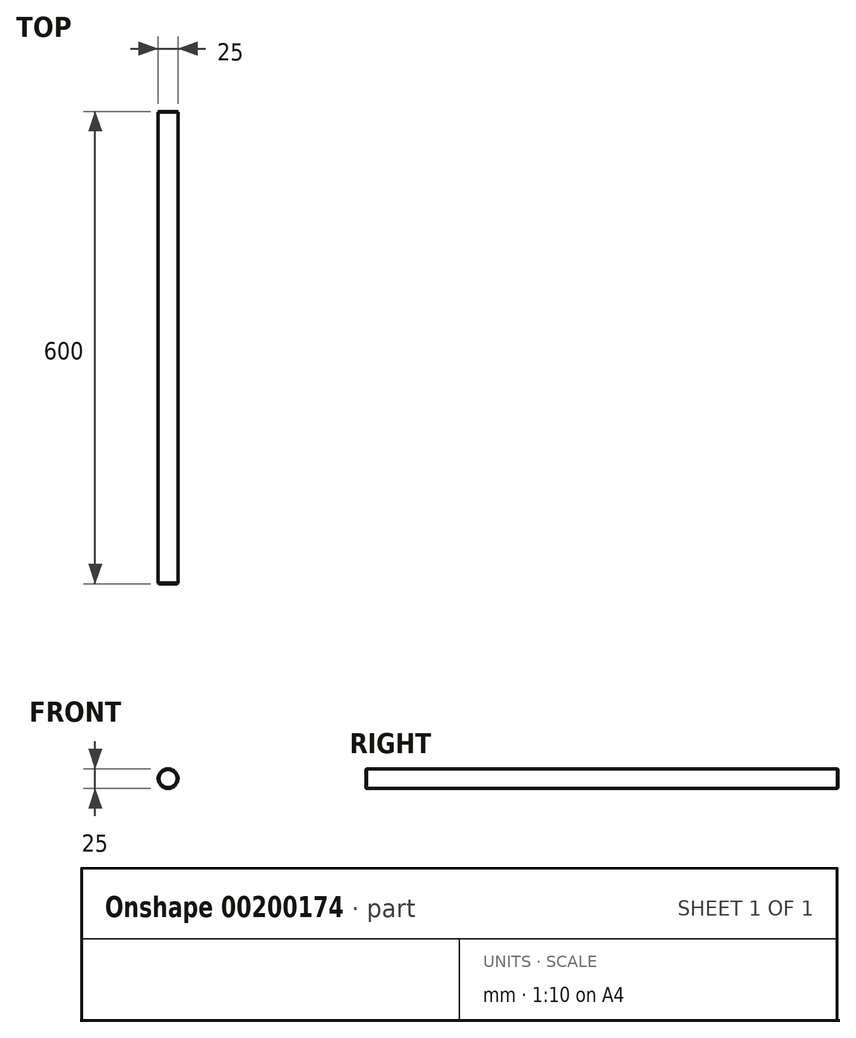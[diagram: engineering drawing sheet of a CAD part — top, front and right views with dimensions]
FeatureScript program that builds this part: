
annotation { "Feature Type Name" : "Feature", "Feature Type Description" : "" }
export const myFeature = defineFeature(function(context is Context, id is Id, definition is map)
    precondition{}
    {
        {
            var Q0;
            Q0=qCreatedBy(makeId("Front.planeOp"),FACE);
            var sketch = newSketch(context, id + "F0", { "sketchPlane" : qUnion([Q0])});
            skCircle(sketch, "E0", {"center": v(0, 0) * mm, "radius": 12.5 * mm});
            skSolve(sketch);
        }
        {
            var Q0;
            Q0 = qSketchRegion(id + "F0", true);
            extrude(context, id + "F1", {"entities" : qUnion([Q0]), "depth" : 600 * mm});
        }
        {
            var Q0;
            Q0=makeQuery(id+"F1.opExtrude","CAP_FACE",FACE,{"disambiguationData":[OSD([sQuery(id+"F0.wireOp",EDGE,"E0")])],"isStart":false});
            chamfer(context, id + "F2", {"entities" : qUnion([Q0]), "width" : 1 * mm, "tangentPropagation" : true});
        }
        {
            var Q0;
            Q0=makeQuery(id+"F1.opExtrude","CAP_EDGE",EDGE,{"disambiguationData":[OSD([sQuery(id+"F0.wireOp",EDGE,"E0")])],"isStart":true});
            chamfer(context, id + "F3", {"entities" : qUnion([Q0]), "width" : 1 * mm, "tangentPropagation" : true});
        }
    });
